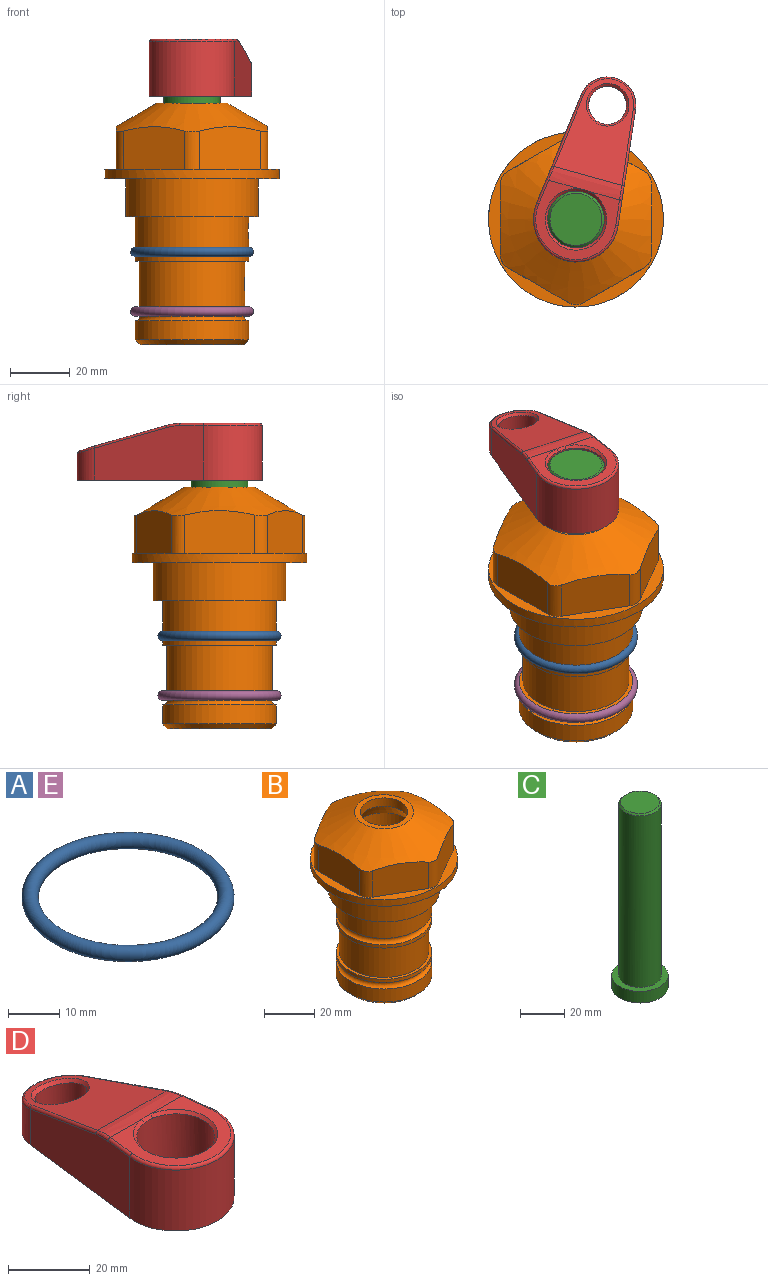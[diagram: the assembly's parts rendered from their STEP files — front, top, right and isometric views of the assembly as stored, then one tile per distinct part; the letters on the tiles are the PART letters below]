
ASSEMBLY  parts=5 mates=4
PART A: 1 faces, bbox 44.7x44.7x3.2 mm
  f0: torus R=19.05mm, axis (0,0,1), area 1193.9mm2
PART B: 36 faces, bbox 58.7x58.7x81 mm
  f0: cylinder r=17.78mm len=35.56mm, axis (0,0,1), area 1670.8mm2, adj f23,f24,f31
  f1: cylinder r=19.05mm len=38.1mm, axis (0,0,1), area 1191.9mm2, adj f26,f27,f30
  f2: plane 58.66x58.66mm, normal (0,0,-1), area 1150.6mm2, adj f3,f28
  f3: cylinder r=29.33mm len=58.66mm, axis (0,0,-1), area 585.1mm2, adj f2,f4
  f4: plane 58.66x58.66mm, normal (0,0,1), area 475.9mm2, adj f3,f5,f6,f7,f8,f9,f10,f11
  f5: plane 20.32x14.34mm, normal (-0.5,0.87,0), area 324.4mm2, adj f4,f15,f16,f17
  f6: plane 20.32x14.34mm, normal (0.5,0.87,0), area 324.4mm2, adj f4,f14,f15,f17
  f7: plane 23.48x14.34mm, normal (1,0,0), area 324.4mm2, adj f4,f13,f14,f17
  f8: plane 20.32x14.34mm, normal (0.5,-0.87,0), area 324.4mm2, adj f4,f12,f13,f17
  f9: plane 20.32x14.34mm, normal (-0.5,-0.87,0), area 324.4mm2, adj f4,f11,f12,f17
  f10: plane 23.48x14.34mm, normal (-1,0,0), area 324.4mm2, adj f4,f11,f16,f17
  f11: cylinder r=5.08mm len=12.85mm, axis (0,0,-1), area 67.2mm2, adj f4,f9,f10,f17
  f12: cylinder r=5.08mm len=12.85mm, axis (0,0,-1), area 67.2mm2, adj f4,f8,f9,f17
  f13: cylinder r=5.08mm len=12.85mm, axis (0,0,-1), area 67.2mm2, adj f4,f7,f8,f17
  f14: cylinder r=5.08mm len=12.85mm, axis (0,0,-1), area 67.2mm2, adj f4,f6,f7,f17
  f15: cylinder r=5.08mm len=12.85mm, axis (0,0,-1), area 67.2mm2, adj f4,f5,f6,f17
  f16: cylinder r=5.08mm len=12.85mm, axis (0,0,-1), area 67.2mm2, adj f4,f5,f10,f17
  f17: cone r=11.73mm half-angle=60deg, axis (0,0,-1), area 2071.8mm2, adj f5,f6,f7,f8,f9,f10,f11,f12
  f18: plane 23.46x23.46mm, normal (0,0,1), area 147.4mm2, adj f17,f35
  f19: plane 34.93x34.93mm, normal (0,0,-1), area 958mm2, adj f29
  f20: cylinder r=19.05mm len=38.1mm, axis (0,0,1), area 760.1mm2, adj f21,f29
  f21: torus R=19.05mm, axis (0,0,1), area 565.3mm2, adj f20,f22
  f22: cylinder r=19.05mm len=38.1mm, axis (0,0,1), area 190mm2, adj f21,f23
  f23: plane 38.1x38.1mm, normal (0,0,1), area 146.9mm2, adj f0,f22
  f24: plane 38.1x38.1mm, normal (0,0,-1), area 146.9mm2, adj f0,f25
  f25: cylinder r=19.05mm len=38.1mm, axis (0,0,1), area 190mm2, adj f24,f26
  f26: torus R=19.05mm, axis (0,0,1), area 565.3mm2, adj f1,f25
  f27: plane 44.45x44.45mm, normal (0,0,-1), area 411.7mm2, adj f1,f28
  f28: cylinder r=22.23mm len=44.45mm, axis (0,0,1), area 1773.5mm2, adj f2,f27
  f29: cone r=19.05mm half-angle=45deg, axis (0,0,1), area 257.5mm2, adj f19,f20
  f30: cylinder r=3.17mm len=6.75mm, axis (-1,0,0), area 128mm2, adj f1,f33
  f31: cylinder r=3.17mm len=6.35mm, axis (-1,0,0), area 102.5mm2, adj f0,f33
  f32: plane 25.4x25.4mm, normal (0,0,1), area 506.7mm2, adj f33
  f33: cylinder r=12.7mm len=66.42mm, axis (0,0,-1), area 5236.2mm2, adj f30,f31,f32,f34
  f34: cone r=9.53mm half-angle=30deg, axis (0,0,-1), area 443.4mm2, adj f33,f35
  f35: cylinder r=9.53mm len=19.05mm, axis (0,0,-1), area 240.9mm2, adj f18,f34
PART C: 6 faces, bbox 25.4x25.4x101.6 mm
  f0: plane 17.46x17.46mm, normal (0,0,1), area 239.5mm2, adj f5
  f1: plane 25.4x25.4mm, normal (0,0,-1), area 506.7mm2, adj f2
  f2: cylinder r=12.7mm len=25.4mm, axis (0,0,1), area 506.7mm2, adj f1,f3
  f3: plane 25.4x25.4mm, normal (0,0,1), area 221.7mm2, adj f2,f4
  f4: cylinder r=9.53mm len=94.46mm, axis (0,0,1), area 5653mm2, adj f3,f5
  f5: cone r=8.73mm half-angle=45deg, axis (0,0,-1), area 64.4mm2, adj f0,f4
PART D: 31 faces, bbox 31.7x65.5x19.8 mm
  f0: plane 39.12x18.26mm, normal (0.99,0.12,0), area 612.2mm2, adj f1,f4,f7,f11,f13,f15
  f1: cylinder r=9.53mm len=18.91mm, axis (0,0,-1), area 296.1mm2, adj f0,f2,f7,f17
  f2: plane 39.12x18.26mm, normal (-0.99,0.12,0), area 612.2mm2, adj f1,f4,f7,f12,f14,f16
  f3: cylinder r=6.35mm len=12.7mm, axis (0,0,-1), area 362.4mm2, adj f7,f18
  f4: cylinder r=14.29mm len=28.58mm, axis (0,0,-1), area 882.2mm2, adj f0,f2,f7,f10
  f5: cylinder r=9.53mm len=19.05mm, axis (0,0,-1), area 1092.6mm2, adj f7,f19,f20
  f6: plane 26.99x23.69mm, normal (0,0,1), area 216.2mm2, adj f9,f10,f11,f12,f19
  f7: plane 63.5x28.58mm, normal (0,0,-1), area 661.8mm2, adj f0,f1,f2,f3,f4,f5,f22,f23
  f8: plane 33.52x23.6mm, normal (0,0.26,0.97), area 486mm2, adj f9,f15,f16,f17,f18
  f9: cylinder r=19.05mm len=24.72mm, axis (1,0,0), area 120.4mm2, adj f6,f8,f13,f14,f20
  f10: torus R=13.49mm, axis (0,0,1), area 59mm2, adj f4,f6,f11,f12
  f11: cylinder r=0.79mm len=8.67mm, axis (0.12,-0.99,0), area 10.8mm2, adj f0,f6,f10,f13
  f12: cylinder r=0.79mm len=8.67mm, axis (0.12,0.99,0), area 10.8mm2, adj f2,f6,f10,f14
  f13: bspline ~4.95x1.42mm, area 6.1mm2, adj f0,f9,f11,f15
  f14: bspline ~4.95x1.42mm, area 6.1mm2, adj f2,f9,f12,f16
  f15: cylinder r=0.79mm len=25.95mm, axis (0.12,-0.96,0.26), area 32.9mm2, adj f0,f8,f13,f17
  f16: cylinder r=0.79mm len=25.95mm, axis (0.12,0.96,-0.26), area 32.9mm2, adj f2,f8,f14,f17
  f17: bspline ~18.91x8.38mm, area 30mm2, adj f1,f8,f15,f16
  f18: bspline ~14.29x14.29mm, area 48.3mm2, adj f3,f8
  f19: cone r=9.53mm half-angle=45deg, axis (0,0,1), area 66.5mm2, adj f5,f6,f20
  f20: bspline ~3.22x0.96mm, area 3.5mm2, adj f5,f9,f19
  f21: plane 2.75x2.72mm, normal (0,0,-1), area 2.9mm2, adj f23,f25,f28
  f22: plane 23.05x15.88mm, normal (-0.99,-0.12,0), area 323.6mm2, adj f7,f25,f26,f27,f28,f29
  f23: plane 23.05x15.88mm, normal (0.99,-0.12,0), area 323.6mm2, adj f7,f21,f25,f27,f28,f30
  f24: cylinder r=9.53mm len=10.69mm, axis (0,0,-1), area 114.7mm2, adj f7,f27,f29,f30
  f25: cylinder r=12.7mm len=20.59mm, axis (0,0,-1), area 381.1mm2, adj f7,f21,f22,f23,f26,f28
  f26: plane 2.75x2.72mm, normal (0,0,-1), area 2.9mm2, adj f22,f25,f28
  f27: plane 19.72x18.37mm, normal (0,-0.26,-0.97), area 291.8mm2, adj f22,f23,f24,f28,f29,f30
  f28: cylinder r=15.88mm len=19.92mm, axis (1,0,0), area 54.8mm2, adj f21,f22,f23,f25,f26,f27
  f29: cylinder r=1.59mm len=11mm, axis (0,0,-1), area 34.7mm2, adj f7,f22,f24,f27
  f30: cylinder r=1.59mm len=11mm, axis (0,0,-1), area 34.7mm2, adj f7,f23,f24,f27
PART E: same geometry as A
PLACE A t=(-12.53,-7.37,10.73)mm
PLACE B t=(-12.53,-7.37,10.73)mm fixed
PLACE C rot(axis=(0,0,-1),15.5deg) t=(-12.53,-7.37,-6.8)mm
PLACE D rot(axis=(0,0,-1),15.5deg) t=(-12.53,-7.37,-6)mm
PLACE E t=(-12.53,-7.37,-9.27)mm
MATE fastened C.f2 <-> D.f4  axis (0,0,1) through (-12.53,-7.37,56.7)mm
MATE fastened E.f0 <-> B.f0  axis (0,0,1) through (-12.53,-7.37,-33.79)mm
MATE fastened A.f0 <-> B.f0  axis (0,0,1) through (-12.53,-7.37,-13.78)mm
MATE cylindrical C.f2 <-> B.f0  axis (0,0,-1) through (-12.53,-7.37,-44.9)mm
